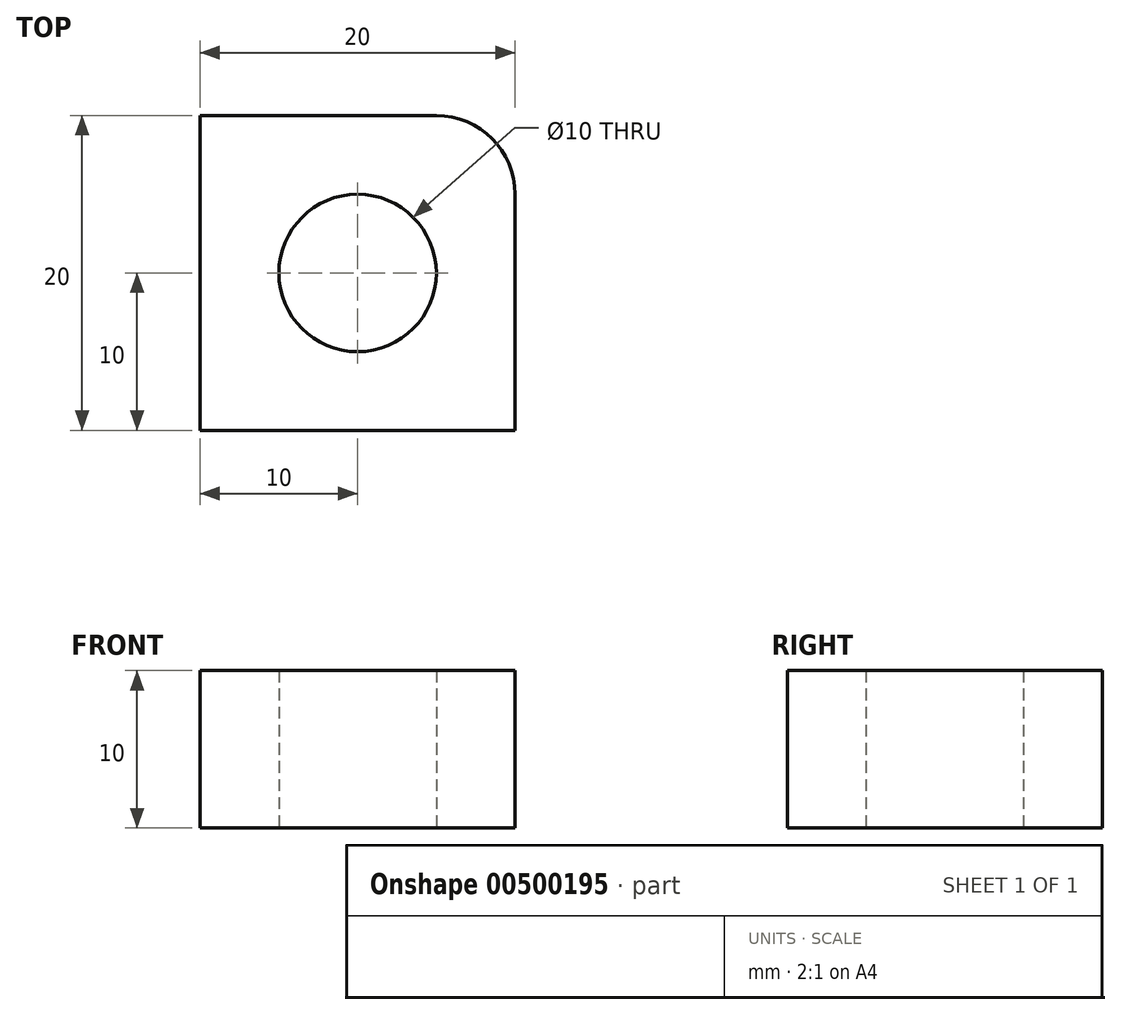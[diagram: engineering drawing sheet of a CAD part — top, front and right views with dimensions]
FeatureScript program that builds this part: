
annotation { "Feature Type Name" : "Feature", "Feature Type Description" : "" }
export const myFeature = defineFeature(function(context is Context, id is Id, definition is map)
    precondition{}
    {
        {
            var Q0;
            Q0=qCreatedBy(makeId("Top.planeOp"),FACE);
            var sketch = newSketch(context, id + "F0", { "sketchPlane" : qUnion([Q0])});
            skLineSegment(sketch, "E0.bottom", {"start": v(0, 0) * mm, "end": v(20, 0) * mm});
            skLineSegment(sketch, "E0.top", {"start": v(0, 20) * mm, "end": v(20, 20) * mm});
            skLineSegment(sketch, "E0.left", {"start": v(0, 0) * mm, "end": v(0, 20) * mm});
            skLineSegment(sketch, "E0.right", {"start": v(20, 0) * mm, "end": v(20, 20) * mm});
            skCircle(sketch, "E1", {"center": v(10, 10) * mm, "radius": 5 * mm});
            skPoint(sketch, "E1.centerSnap0", {"position": v(20, 10) * mm});
            skPoint(sketch, "E1.centerSnap1", {"position": v(10, 20) * mm});
            skSolve(sketch);
        }
        {
            var Q0;
            Q0=makeQuery(id+"F0.imprint","IMPRINT",FACE,{"disambiguationData":[TD([[makeQuery(id+"F0.imprint","IMPRINT",EDGE,{"derivedFrom":sQuery(id+"F0.wireOp",EDGE,"E0.bottom")}),1.0]])]});
            extrude(context, id + "F1", {"entities" : qUnion([Q0]), "depth" : 10 * mm});
        }
        {
            var Q0;
            Q0=makeQuery(id+"F1.opExtrude","SWEPT_EDGE",EDGE,{"disambiguationData":[OSD([sQuery(id+"F0.wireOp",EDGE,"E0.top"),sQuery(id+"F0.wireOp",EDGE,"E0.right")])]});
            fillet(context, id + "F2", {"entities" : qUnion([Q0]), "radius" : 5 * mm, "tangentPropagation" : true, "allowEdgeOverflow" : false});
        }
    });
